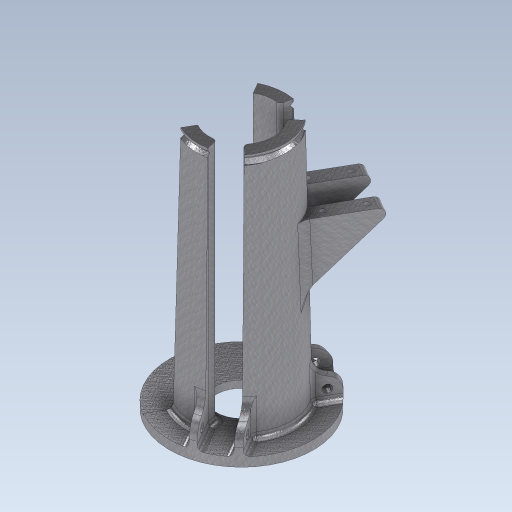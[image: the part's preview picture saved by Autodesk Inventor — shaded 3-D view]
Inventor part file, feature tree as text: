
AUTODESK INVENTOR PART (.ipt)
format: ipt  version: 2023 (Build 270158000, 158)  size: 1,499,648 bytes
history: native  units: in
note: dims shown in document units (in); Inventor stores cm internally (conversion verified against a paired STEP export)
features: projected_geometry x8, sketch x7, extrude x5, revolve x5, fillet x3, hole x2, direct_edit x2, pattern_circular x1, plane x1
ambient origin geometry x8: Origin, YZ Plane, XZ Plane, XY Plane, X Axis, Y Axis, Z Axis, Center Point
bodies: Solid1 (feature_tree)
feature tree (34):
  sketch  "Sketch2"  dims[d0=1.0in d1=1.4038in]
  extrude  "Extrusion1"  Depth=1.4038in
  extrude  "Extrusion2"  TaperAngle=120.0deg  [1 undecoded]
  extrude  "Extrusion3"  Depth=0.481in
  hole  "Hole1"  [1 undecoded]
  pattern_circular  "Circular Pattern1"  Count=14  [1 undecoded]
  sketch  "Sketch5"  dims[d6=0.8987in d7=0.7874in d9=120.0deg]
  fillet  "Fillet1"  Radius=0.1378in
  extrude  "Extrusion5"  Depth=0.1378in
  plane  "Work Plane1"
  direct_edit  "Direct Edit3"
  extrude  "Extrusion6"  Depth=0.5906in
  hole  "Hole2"  [1 undecoded]
  direct_edit  "Direct Edit2"
  fillet  "Fillet2"  Radius=0.7874in
  fillet  "Fillet3"  Radius=0.1181in
  revolve  "Revolution1"  [1 undecoded]
  sketch  "Sketch3"  dims[d2=3.1496in d3=120.0deg]
  projected_geometry  "Projected Loop1"
  projected_geometry  "Projected Loop2"
  projected_geometry  "Projected Loop3"
  projected_geometry  "Projected Loop4"
  sketch  "Sketch4"  dims[d4=0.5906in d5=0.481in]
  projected_geometry  "Projected Loop5"
  sketch  "Sketch7"  dims[d11=0.8987in]
  sketch  "Sketch8"  dims[d13=120.0deg]
  projected_geometry  "Projected Loop6"
  projected_geometry  "Projected Loop7"
  sketch  "Sketch10"  dims[d14=0.1969in d15=0.0in d17=5.5118in d18=0.0in d19=0.1378in d20=0.1378in d21=0.5906in d22=0.4961in d23=0.0in d24=0.7874in d25=120.0deg d27=0.1181in d28=0.1772in d29=0.2362in d30=0.1575in d31=0.0787in d32=90.0deg d33=0.315in d34=0.8108in d35=0.3937in d39=1.0945in d40=0.0787in d41=0.0394in d42=0.0in d43=0.1181in d44=0.315in d45=-1.6614in d46=0.3228in d47=1.2795in d48=0.7087in d49=1.2644in d50=0.1173in d51=1.378in d52=0.0in d54=-0.323in d55=0.2362in d56=0.2362in d57=0.1575in d58=0.0787in d59=90.0deg d60=1.2598in d61=0.8108in d63=0.0103in d64=-0.0103in d65=-0.0103in d66=0.1181in d67=0.0787in d68=360.0deg d69=0.0344in]
  projected_geometry  "Projected Loop8"
  revolve  "Rotate2"  [1 undecoded]
  revolve  "Rotate3"  [1 undecoded]
  revolve  "Rotate4"  [1 undecoded]
  revolve  "Rotate5"  [1 undecoded]
note: 9 required parameter values undecoded (feature->parameter linkage not recoverable at this tier; creation-order binding heuristic only, values carry confidence <= 0.55)